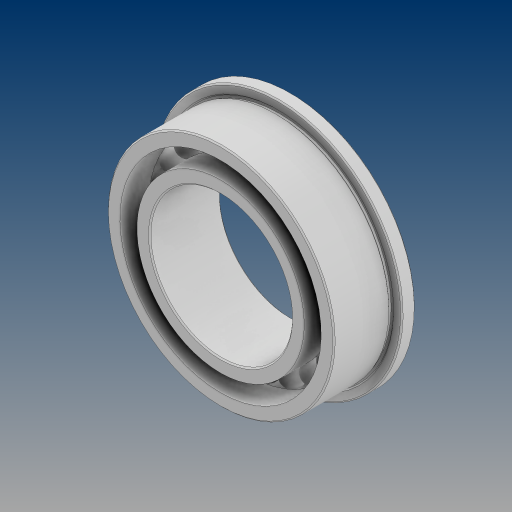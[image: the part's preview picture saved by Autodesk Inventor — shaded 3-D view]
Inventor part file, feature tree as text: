
AUTODESK INVENTOR PART (.ipt)
format: ipt  version: 2024.3 (Build 283343000, 343)  size: 992,256 bytes
history: native  units: in
note: dims shown in document units (in); Inventor stores cm internally (conversion verified against a paired STEP export)
features: other x22, fillet x2, revolve x1
ambient origin geometry x8: Origin, YZ Plane, XZ Plane, XY Plane, X Axis, Y Axis, Z Axis, Center Point
bodies: Solid1 (feature_tree), Solid2 (feature_tree), Solid3 (feature_tree), Solid4 (feature_tree), Solid5 (feature_tree), Solid6 (feature_tree), Solid7 (feature_tree), Solid8 (feature_tree), Solid9 (feature_tree), Solid10 (feature_tree), Solid11 (feature_tree), Solid12 (feature_tree), Solid13 (feature_tree), Solid14 (feature_tree), Solid15 (feature_tree), Solid16 (feature_tree), Solid17 (feature_tree), Solid18 (feature_tree), Solid19 (feature_tree), Solid20 (feature_tree), Solid21 (feature_tree), Solid22 (feature_tree), Solid23 (feature_tree), Solid24 (feature_tree), Solid25 (feature_tree)
feature tree (25):
  fillet  "Fillet1"  [1 undecoded]
  fillet  "Fillet2"  [1 undecoded]
  revolve  "Revolve3"  [1 undecoded]
  other  "CirPattern3[1]"
  other  "CirPattern3[2]"
  other  "CirPattern3[3]"
  other  "CirPattern3[4]"
  other  "CirPattern3[5]"
  other  "CirPattern3[6]"
  other  "CirPattern3[7]"
  other  "CirPattern3[8]"
  other  "CirPattern3[9]"
  other  "CirPattern3[10]"
  other  "CirPattern3[11]"
  other  "CirPattern3[12]"
  other  "CirPattern3[13]"
  other  "CirPattern3[14]"
  other  "CirPattern3[15]"
  other  "CirPattern3[16]"
  other  "CirPattern3[17]"
  other  "CirPattern3[18]"
  other  "CirPattern3[19]"
  other  "CirPattern3[20]"
  other  "CirPattern3[21]"
  other  "CirPattern3[22]"
note: 3 required parameter values undecoded (feature->parameter linkage not recoverable at this tier; creation-order binding heuristic only, values carry confidence <= 0.55)
